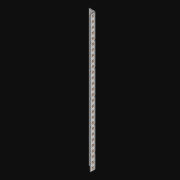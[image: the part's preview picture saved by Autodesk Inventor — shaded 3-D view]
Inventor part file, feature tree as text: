
AUTODESK INVENTOR PART (.ipt)
format: ipt  version: 2021 (Build 250183000, 183)  size: 1,286,144 bytes
history: native  units: in
note: dims shown in document units (in); Inventor stores cm internally (conversion verified against a paired STEP export)
features: extrude x58, other x56, sketch x4, pattern_linear x2, sheet_metal_op x1
ambient origin geometry x8: Origin, YZ Plane, XZ Plane, XY Plane, X Axis, Y Axis, Z Axis, Center Point
bodies: Solid1 (feature_tree)
feature tree (121):
  pattern_linear  "Rectangular Pattern1"  Spacing1=0.5in  [1 undecoded]
  pattern_linear  "Rectangular Pattern3"  Count1=28  [1 undecoded]
  extrude  "Extrusion1"  Depth=0.5in
  extrude  "Extrusion2"  Depth=0.5in
  sketch  "Sketch1"  dims[d0=0.182in]
  other  "Srf1"
  sketch  "Sketch3"  dims[d1=0.063in d2=0.0in]
  other  "Srf3"
  other  "Srf4"
  other  "Srf5"
  other  "Srf6"
  other  "Srf7"
  other  "Srf8"
  other  "Srf9"
  other  "Srf10"
  other  "Srf11"
  other  "Srf12"
  other  "Srf13"
  other  "Srf14"
  other  "Srf15"
  other  "Srf16"
  other  "Srf17"
  other  "Srf18"
  other  "Srf19"
  other  "Srf20"
  other  "Srf21"
  other  "Srf22"
  other  "Srf23"
  other  "Srf24"
  other  "Srf25"
  other  "Srf26"
  other  "Srf27"
  other  "Srf28"
  other  "Srf29"
  other  "Srf30"
  other  "Srf142"
  other  "Srf143"
  other  "Srf144"
  other  "Srf145"
  other  "Srf146"
  other  "Srf147"
  other  "Srf148"
  other  "Srf149"
  other  "Srf150"
  other  "Srf151"
  other  "Srf152"
  other  "Srf153"
  other  "Srf154"
  other  "Srf155"
  other  "Srf156"
  other  "Srf157"
  other  "Srf158"
  other  "Srf159"
  other  "Srf160"
  other  "Srf161"
  other  "Srf162"
  other  "Srf163"
  other  "Srf164"
  other  "Srf165"
  other  "Srf166"
  other  "Srf167"
  other  "Srf168"
  sketch  "Sketch4"  dims[d6=0.182in]
  sketch  "Sketch5"  dims[d7=0.063in d8=0.0in d11=0.5in d12=0.3937in d14=0.5in d18=11.0236in d20=0.5in d21=3.5in d22=0.0in d23=0.841in d24=0.0in]
  sheet_metal_op  "Fold1"
  extrude  "ExtrusionSrf1"  TaperAngle=0.0deg  [1 undecoded]
  extrude  "ExtrusionSrf3"  Depth=0.5in TaperAngle=0.0deg
  extrude  "ExtrusionSrf4"  [1 undecoded]
  extrude  "ExtrusionSrf5"  [1 undecoded]
  extrude  "ExtrusionSrf6"  [1 undecoded]
  extrude  "ExtrusionSrf7"  [1 undecoded]
  extrude  "ExtrusionSrf8"  [1 undecoded]
  extrude  "ExtrusionSrf9"  [1 undecoded]
  extrude  "ExtrusionSrf10"  [1 undecoded]
  extrude  "ExtrusionSrf11"  [1 undecoded]
  extrude  "ExtrusionSrf12"  [1 undecoded]
  extrude  "ExtrusionSrf13"  [1 undecoded]
  extrude  "ExtrusionSrf14"  [1 undecoded]
  extrude  "ExtrusionSrf15"  [1 undecoded]
  extrude  "ExtrusionSrf16"  [1 undecoded]
  extrude  "ExtrusionSrf17"  [1 undecoded]
  extrude  "ExtrusionSrf18"  [1 undecoded]
  extrude  "ExtrusionSrf19"  [1 undecoded]
  extrude  "ExtrusionSrf20"  [1 undecoded]
  extrude  "ExtrusionSrf21"  [1 undecoded]
  extrude  "ExtrusionSrf22"  [1 undecoded]
  extrude  "ExtrusionSrf23"  [1 undecoded]
  extrude  "ExtrusionSrf24"  [1 undecoded]
  extrude  "ExtrusionSrf25"  [1 undecoded]
  extrude  "ExtrusionSrf26"  [1 undecoded]
  extrude  "ExtrusionSrf27"  [1 undecoded]
  extrude  "ExtrusionSrf28"  [1 undecoded]
  extrude  "ExtrusionSrf29"  [1 undecoded]
  extrude  "ExtrusionSrf30"  [1 undecoded]
  extrude  "ExtrusionSrf142"  [1 undecoded]
  extrude  "ExtrusionSrf143"  [1 undecoded]
  extrude  "ExtrusionSrf144"  [1 undecoded]
  extrude  "ExtrusionSrf145"  [1 undecoded]
  extrude  "ExtrusionSrf146"  [1 undecoded]
  extrude  "ExtrusionSrf147"  [1 undecoded]
  extrude  "ExtrusionSrf148"  [1 undecoded]
  extrude  "ExtrusionSrf149"  [1 undecoded]
  extrude  "ExtrusionSrf150"  [1 undecoded]
  extrude  "ExtrusionSrf151"  [1 undecoded]
  extrude  "ExtrusionSrf152"  [1 undecoded]
  extrude  "ExtrusionSrf153"  [1 undecoded]
  extrude  "ExtrusionSrf154"  [1 undecoded]
  extrude  "ExtrusionSrf155"  [1 undecoded]
  extrude  "ExtrusionSrf156"  [1 undecoded]
  extrude  "ExtrusionSrf157"  [1 undecoded]
  extrude  "ExtrusionSrf158"  [1 undecoded]
  extrude  "ExtrusionSrf159"  [1 undecoded]
  extrude  "ExtrusionSrf160"  [1 undecoded]
  extrude  "ExtrusionSrf161"  [1 undecoded]
  extrude  "ExtrusionSrf162"  [1 undecoded]
  extrude  "ExtrusionSrf163"  [1 undecoded]
  extrude  "ExtrusionSrf164"  [1 undecoded]
  extrude  "ExtrusionSrf165"  [1 undecoded]
  extrude  "ExtrusionSrf166"  [1 undecoded]
  extrude  "ExtrusionSrf167"  [1 undecoded]
  extrude  "ExtrusionSrf168"  [1 undecoded]
note: 57 required parameter values undecoded (feature->parameter linkage not recoverable at this tier; creation-order binding heuristic only, values carry confidence <= 0.55)
